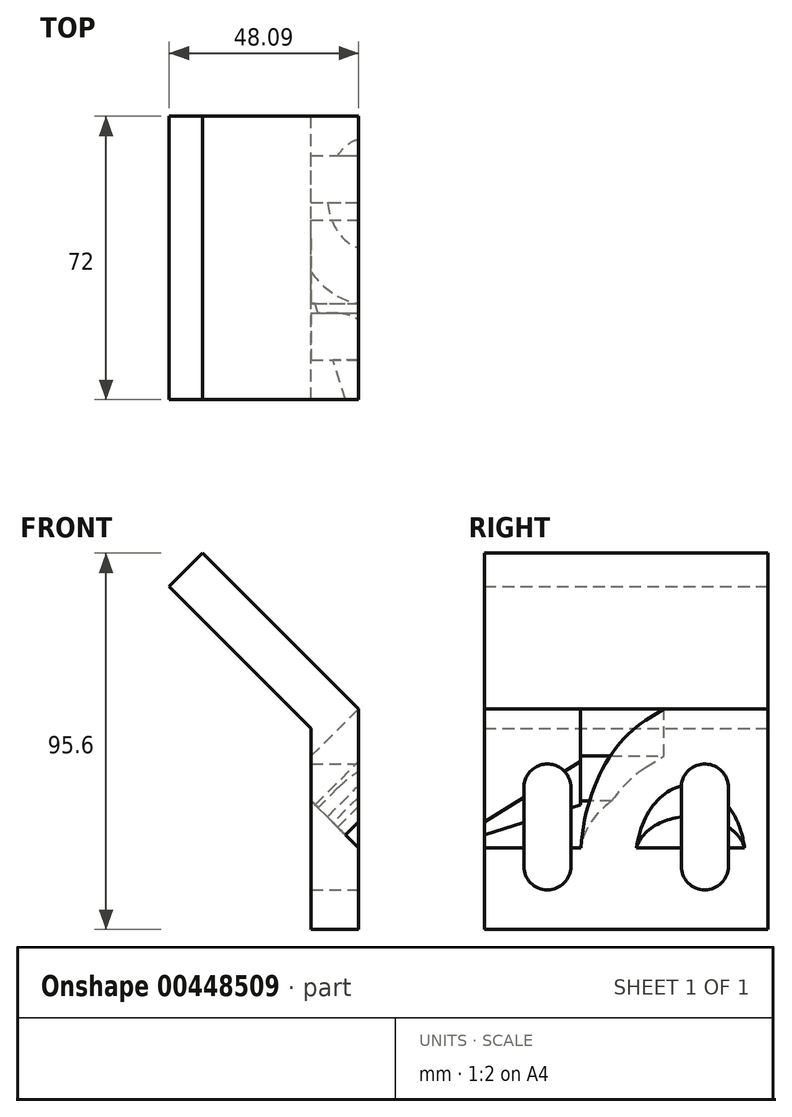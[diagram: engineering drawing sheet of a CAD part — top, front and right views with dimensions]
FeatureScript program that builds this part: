
annotation { "Feature Type Name" : "Feature", "Feature Type Description" : "" }
export const myFeature = defineFeature(function(context is Context, id is Id, definition is map)
    precondition{}
    {
        {
            var Q0;
            Q0=qCreatedBy(makeId("Front.planeOp"),FACE);
            var sketch = newSketch(context, id + "F0", { "sketchPlane" : qUnion([Q0])});
            skLineSegment(sketch, "E0", {"start": v(26.02, 14.2) * mm, "end": v(26.02, -41.8) * mm});
            skLineSegment(sketch, "E1", {"start": v(14.02, 9.22) * mm, "end": v(14.02, -41.8) * mm});
            skLineSegment(sketch, "E2", {"start": v(14.02, -41.8) * mm, "end": v(26.02, -41.8) * mm});
            skLineSegment(sketch, "E3", {"start": v(-22.07, 45.3) * mm, "end": v(-13.58, 53.79) * mm});
            skLineSegment(sketch, "E4", {"start": v(-13.58, 53.79) * mm, "end": v(26.02, 14.2) * mm});
            skLineSegment(sketch, "E5", {"start": v(14.02, 9.22) * mm, "end": v(-22.07, 45.3) * mm});
            skSolve(sketch);
        }
        {
            var Q0;
            Q0 = qSketchRegion(id + "F0", true);
            extrude(context, id + "F1", {"entities" : qUnion([Q0]), "depth" : (40 + 32) * mm});
        }
        {
            var Q0;
            Q0=makeQuery(id+"F1.opExtrude","SWEPT_FACE",FACE,{"disambiguationData":[OSD([sQuery(id+"F0.wireOp",EDGE,"E4")])]});
            var sketch = newSketch(context, id + "F2", { "sketchPlane" : qUnion([Q0])});
            skPoint(sketch, "E6.centerSnap0", {"position": v(-47.64, -36) * mm});
            skCircle(sketch, "E7", {"center": v(-19.64, -36) * mm, "radius": 14 * mm});
            skCircle(sketch, "E8", {"center": v(-19.64, -36) * mm, "radius": 28 * mm});
            skSolve(sketch);
        }
        {
            var Q0;
            Q0=makeQuery(id+"F2.imprint","IMPRINT",FACE,{"disambiguationData":[TD([[makeQuery(id+"F2.imprint","IMPRINT",EDGE,{"derivedFrom":sQuery(id+"F2.wireOp",EDGE,"E7")}),1.0]])]});
            extrude(context, id + "F3", {"entities" : qUnion([Q0]), "operationType" : NewBodyOperationType.REMOVE, "oppositeDirection" : true, "depth" : 25 * mm});
        }
        {
            var Q0;
            Q0=makeQuery(id+"F2.imprint","IMPRINT",FACE,{"disambiguationData":[TD([[makeQuery(id+"F2.imprint","IMPRINT",EDGE,{"derivedFrom":sQuery(id+"F2.wireOp",EDGE,"E7")}),-1.0]])]});
            var sketch = newSketch(context, id + "F4", { "sketchPlane" : qUnion([Q0])});
            skLineSegment(sketch, "E9", {"start": v(381.38, -76.3) * mm, "end": v(137.08, -34.45) * mm});
            skLineSegment(sketch, "E10", {"start": v(512.1, 94.07) * mm, "end": v(271.74, 123.74) * mm});
            skLineSegment(sketch, "E11", {"start": v(1261.2, 152.45) * mm, "end": v(1662.3, 109.52) * mm});
            skLineSegment(sketch, "E12", {"start": v(781.17, 117.09) * mm, "end": v(1738.54, 33.98) * mm});
            skLineSegment(sketch, "E13", {"start": v(-88.44, -36) * mm, "end": v(-7.64, -72) * mm});
            skLineSegment(sketch, "E14", {"start": v(-47.64, -36) * mm, "end": v(-47.64, -36) * mm});
            skPoint(sketch, "E15.0", {"position": v(8.36, -72) * mm});
            skPoint(sketch, "E16.0", {"position": v(8.36, 0) * mm});
            skLineSegment(sketch, "E17", {"start": v(8.36, -72) * mm, "end": v(-7.64, -72) * mm});
            skLineSegment(sketch, "E18", {"start": v(8.36, 0) * mm, "end": v(-7.64, 0) * mm});
            skLineSegment(sketch, "E19", {"start": v(-88.44, -36) * mm, "end": v(-7.64, 0) * mm});
            skSolve(sketch);
        }
        {
            var Q0;
            {var subQ1=sQuery(id+"F0.wireOp",EDGE,"E4");var subQ6=makeQuery(id+"F1.opExtrude","CAP_EDGE",EDGE,{"disambiguationData":[OSD([subQ1])],"isStart":true});Q0=makeQuery(id+"F2.imprint","IMPRINT",FACE,{"disambiguationData":[TD([[makeQuery(id+"F2.imprint","IMPRINT",EDGE,{"derivedFrom":subQ6}),-1.0]])]});}
            var sketch = newSketch(context, id + "F5", { "sketchPlane" : qUnion([Q0])});
            skPoint(sketch, "E20.0", {"position": v(-48.04, -18) * mm});
            skPoint(sketch, "E21.0", {"position": v(-7.64, 0) * mm});
            skPoint(sketch, "E22.0", {"position": v(-48.04, -54) * mm});
            skPoint(sketch, "E23.0", {"position": v(-7.64, -72) * mm});
            skLineSegment(sketch, "E24", {"start": v(-7.64, -72) * mm, "end": v(-48.04, -54) * mm});
            skLineSegment(sketch, "E25", {"start": v(-48.04, -18) * mm, "end": v(-7.64, 0) * mm});
            skCircle(sketch, "E26.0", {"center": v(-19.64, -36) * mm, "radius": 14 * mm});
            skCircle(sketch, "E27.0", {"center": v(-19.64, -36) * mm, "radius": 28 * mm});
            skLineSegment(sketch, "E28.0", {"start": v(-47.64, -72) * mm, "end": v(-47.64, 0) * mm});
            skLineSegment(sketch, "E29.0", {"start": v(-47.64, -72) * mm, "end": v(8.36, -72) * mm});
            skLineSegment(sketch, "E30.0", {"start": v(8.36, -72) * mm, "end": v(8.36, 0) * mm});
            skLineSegment(sketch, "E31.0", {"start": v(8.36, 0) * mm, "end": v(-7.64, 0) * mm});
            skLineSegment(sketch, "E32.0", {"start": v(-47.64, 0) * mm, "end": v(8.36, 0) * mm});
            skSolve(sketch);
        }
        {
            var Q0;
            {var subQ0=sQuery(id+"F5.wireOp",EDGE,"E28.0");var subQ1=sQuery(id+"F5.wireOp",EDGE,"E25");var subQ2=makeQuery(id+"F5.imprint","INTERSECT",VERTEX,{"derivedFrom":[subQ1,subQ0]});Q0=makeQuery(id+"F5.imprint","IMPRINT",FACE,{"disambiguationData":[TD([[makeQuery(id+"F5.imprint","IMPRINT",EDGE,{"disambiguationData":[TD([[subQ2,-1.0]])],"derivedFrom":subQ1}),1.0]])]});}
            var Q1;
            {var subQ0=sQuery(id+"F5.wireOp",EDGE,"E29.0");var subQ1=sQuery(id+"F5.wireOp",EDGE,"E24");var subQ2=makeQuery(id+"F5.imprint","INTERSECT",VERTEX,{"derivedFrom":[subQ1,subQ0]});Q1=makeQuery(id+"F5.imprint","IMPRINT",FACE,{"disambiguationData":[TD([[makeQuery(id+"F5.imprint","IMPRINT",EDGE,{"disambiguationData":[TD([[subQ2,-1.0]])],"derivedFrom":subQ1}),1.0]])]});}
            var Q2;
            {var subQ0=sQuery(id+"F5.wireOp",EDGE,"E28.0");var subQ1=sQuery(id+"F5.wireOp",EDGE,"E24");var subQ2=makeQuery(id+"F5.imprint","INTERSECT",VERTEX,{"derivedFrom":[subQ1,subQ0]});Q2=makeQuery(id+"F5.imprint","IMPRINT",FACE,{"disambiguationData":[TD([[makeQuery(id+"F5.imprint","IMPRINT",EDGE,{"disambiguationData":[TD([[subQ2,1.0]])],"derivedFrom":subQ1}),-1.0]])]});}
            var Q3;
            {var subQ0=sQuery(id+"F4.wireOp",EDGE,"E19");var subQ1=sQuery(id+"F4.wireOp",EDGE,"E13");var subQ2=makeQuery(id+"F4.imprint","INTERSECT",VERTEX,{"derivedFrom":[subQ1,subQ0]});Q3=makeQuery(id+"F4.imprint","IMPRINT",FACE,{"disambiguationData":[TD([[makeQuery(id+"F4.imprint","IMPRINT",EDGE,{"disambiguationData":[TD([[subQ2,-1.0]])],"derivedFrom":subQ1}),1.0]])]});}
            extrude(context, id + "F6", {"entities" : qUnion([Q0, Q1, Q2, Q3]), "operationType" : NewBodyOperationType.REMOVE, "oppositeDirection" : true, "depth" : 25 * mm});
        }
        {
            var Q0;
            Q0=makeQuery(id+"F1.opExtrude","SWEPT_FACE",FACE,{"disambiguationData":[OSD([sQuery(id+"F0.wireOp",EDGE,"E0")])]});
            var sketch = newSketch(context, id + "F7", { "sketchPlane" : qUnion([Q0])});
            skLineSegment(sketch, "E33", {"start": v(-36, -41.8) * mm, "end": v(-36, 14.2) * mm});
            skLineSegment(sketch, "E34", {"start": v(-36, -41.8) * mm, "end": v(-56, -41.8) * mm});
            skLineSegment(sketch, "E35", {"start": v(-56, -41.8) * mm, "end": v(-16, -41.8) * mm});
            skLineSegment(sketch, "E36", {"start": v(-72, -23.16) * mm, "end": v(-72, -3.16) * mm});
            skCircle(sketch, "E37", {"center": v(-56, -25.8) * mm, "radius": 6 * mm});
            skCircle(sketch, "E38", {"center": v(-16, -25.8) * mm, "radius": 6 * mm});
            skCircle(sketch, "E39", {"center": v(-56, -5.8) * mm, "radius": 6 * mm});
            skCircle(sketch, "E40", {"center": v(-16, -5.8) * mm, "radius": 6 * mm});
            skLineSegment(sketch, "E41", {"start": v(-62, -5.8) * mm, "end": v(-62, -25.8) * mm});
            skLineSegment(sketch, "E42", {"start": v(-50, -5.8) * mm, "end": v(-50, -25.8) * mm});
            skLineSegment(sketch, "E43", {"start": v(-22, -5.8) * mm, "end": v(-22, -25.8) * mm});
            skLineSegment(sketch, "E44", {"start": v(-22, -25.8) * mm, "end": v(-10, -25.8) * mm});
            skLineSegment(sketch, "E45", {"start": v(-10, -25.8) * mm, "end": v(-10, -5.8) * mm});
            skSolve(sketch);
        }
        {
            var Q0;
            Q0 = qSketchRegion(id + "F7", true);
            extrude(context, id + "F8", {"entities" : qUnion([Q0]), "operationType" : NewBodyOperationType.REMOVE, "oppositeDirection" : true, "depth" : 25 * mm});
        }
    });
